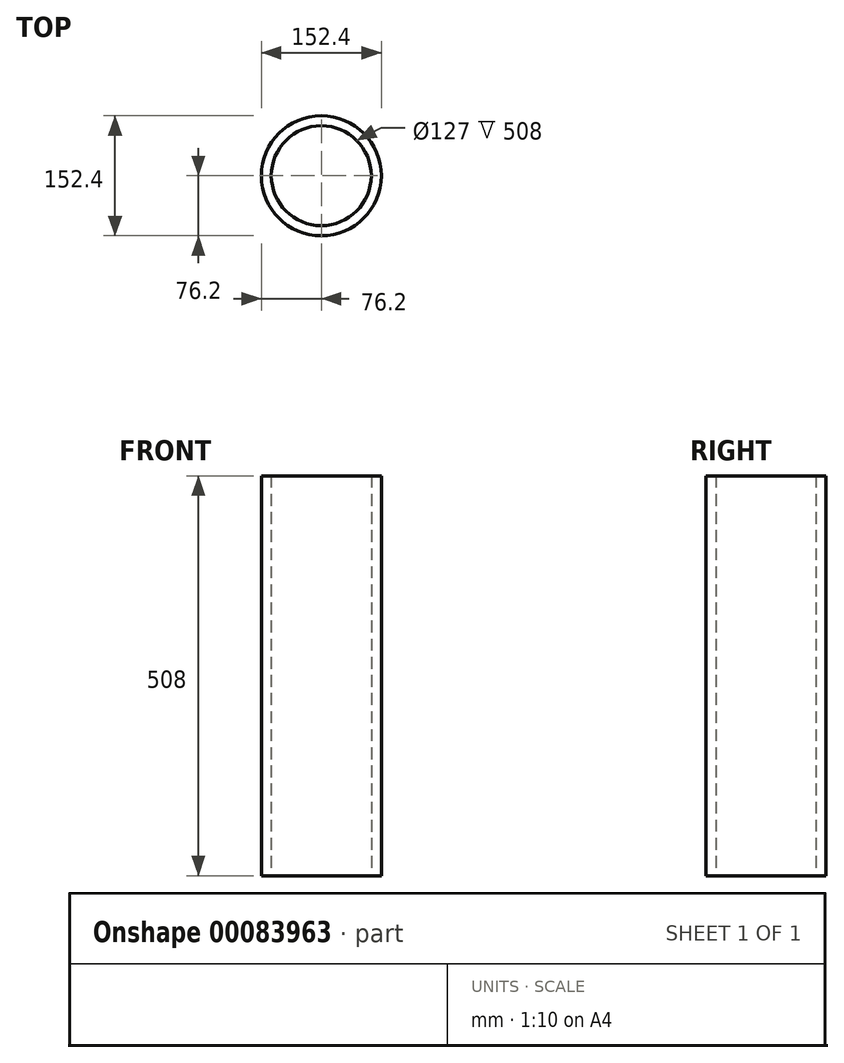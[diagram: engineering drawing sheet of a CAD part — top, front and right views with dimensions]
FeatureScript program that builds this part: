
annotation { "Feature Type Name" : "Feature", "Feature Type Description" : "" }
export const myFeature = defineFeature(function(context is Context, id is Id, definition is map)
    precondition{}
    {
        {
            var Q0;
            Q0=qCreatedBy(makeId("Top.planeOp"),FACE);
            var sketch = newSketch(context, id + "F0", { "sketchPlane" : qUnion([Q0])});
            skCircle(sketch, "E0", {"center": v(0, 0) * mm, "radius": 76.2 * mm});
            skCircle(sketch, "E1", {"center": v(0, 0) * mm, "radius": 63.5 * mm});
            skSolve(sketch);
        }
        {
            var Q0;
            Q0=makeQuery(id+"F0.imprint","IMPRINT",FACE,{"disambiguationData":[TD([[makeQuery(id+"F0.imprint","IMPRINT",EDGE,{"derivedFrom":sQuery(id+"F0.wireOp",EDGE,"E0")}),1.0]])]});
            extrude(context, id + "F1", {"entities" : qUnion([Q0]), "depth" : 508 * mm});
        }
    });
